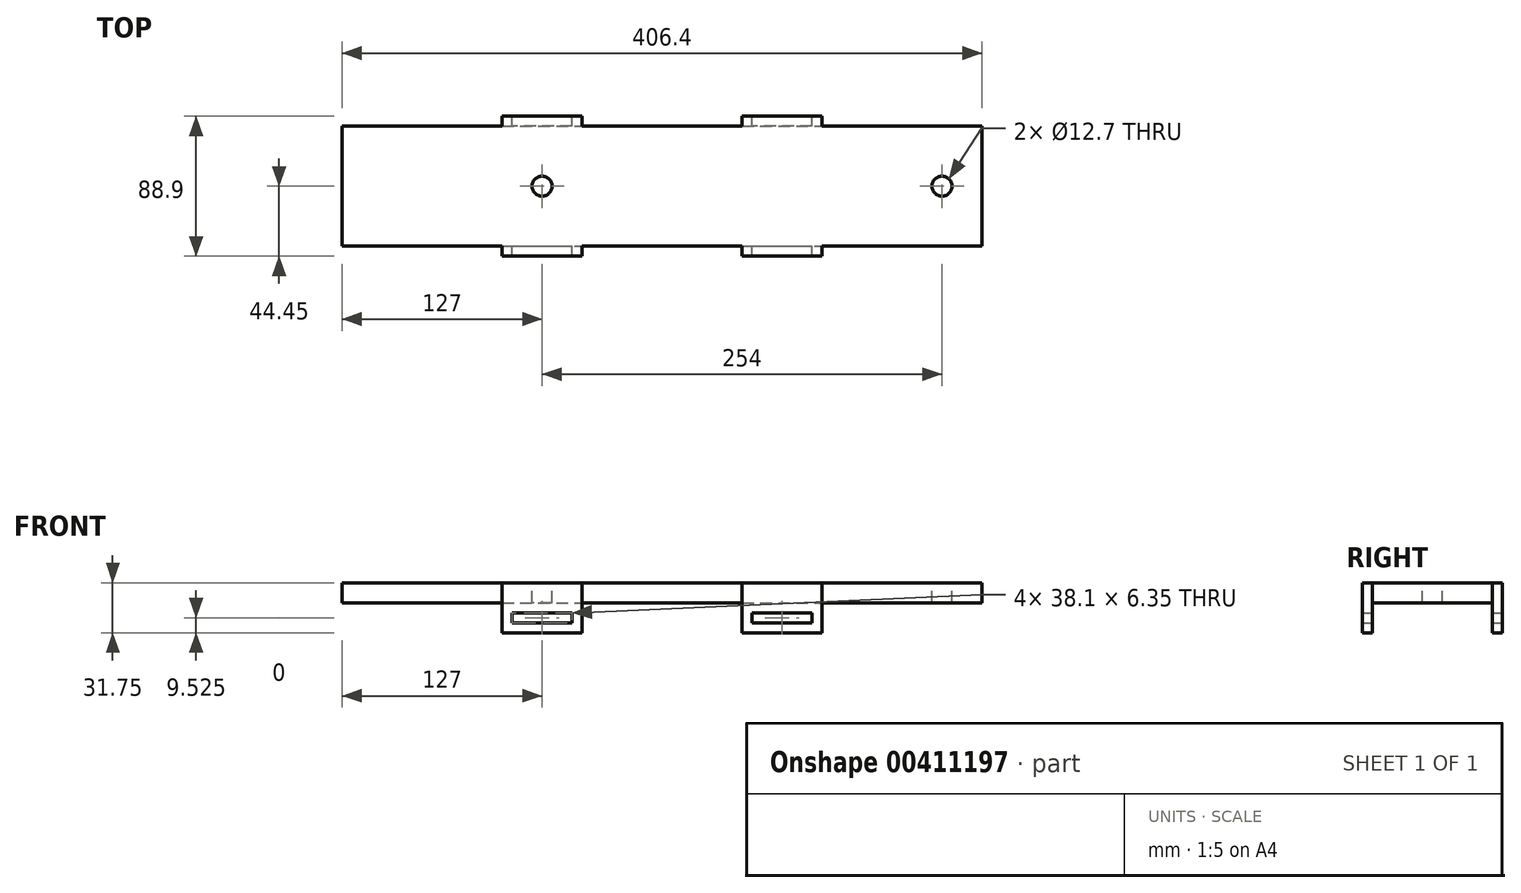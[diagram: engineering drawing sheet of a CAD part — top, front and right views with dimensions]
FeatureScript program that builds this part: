
annotation { "Feature Type Name" : "Feature", "Feature Type Description" : "" }
export const myFeature = defineFeature(function(context is Context, id is Id, definition is map)
    precondition{}
    {
        {
            var Q0;
            Q0=qCreatedBy(makeId("Top.planeOp"),FACE);
            var sketch = newSketch(context, id + "F0", { "sketchPlane" : qUnion([Q0])});
            skLineSegment(sketch, "E0.bottom", {"start": v(-203.2, 38.1) * mm, "end": v(203.2, 38.1) * mm});
            skLineSegment(sketch, "E0.top", {"start": v(-203.2, -38.1) * mm, "end": v(203.2, -38.1) * mm});
            skLineSegment(sketch, "E0.left", {"start": v(-203.2, 38.1) * mm, "end": v(-203.2, -38.1) * mm});
            skLineSegment(sketch, "E0.right", {"start": v(203.2, 38.1) * mm, "end": v(203.2, -38.1) * mm});
            skPoint(sketch, "E0.middle", {"position": v(0, 0) * mm});
            skSolve(sketch);
        }
        {
            var Q0;
            Q0 = qSketchRegion(id + "F0", true);
            extrude(context, id + "F1", {"entities" : qUnion([Q0]), "depth" : 6.35 * mm});
        }
        {
            var Q0;
            Q0=makeQuery(id+"F1.opExtrude","SWEPT_FACE",FACE,{"disambiguationData":[OSD([sQuery(id+"F0.wireOp",EDGE,"E0.top")])]});
            var sketch = newSketch(context, id + "F2", { "sketchPlane" : qUnion([Q0])});
            skLineSegment(sketch, "E1.bottom", {"start": v(50.8, 6.35) * mm, "end": v(101.6, 6.35) * mm});
            skLineSegment(sketch, "E1.top", {"start": v(50.8, -19.05) * mm, "end": v(101.6, -19.05) * mm});
            skLineSegment(sketch, "E1.left", {"start": v(50.8, 6.35) * mm, "end": v(50.8, -19.05) * mm});
            skLineSegment(sketch, "E1.right", {"start": v(101.6, 6.35) * mm, "end": v(101.6, -19.05) * mm});
            skLineSegment(sketch, "E2.bottom", {"start": v(-50.8, 6.35) * mm, "end": v(-101.6, 6.35) * mm});
            skLineSegment(sketch, "E2.top", {"start": v(-50.8, -19.05) * mm, "end": v(-101.6, -19.05) * mm});
            skLineSegment(sketch, "E2.left", {"start": v(-50.8, 6.35) * mm, "end": v(-50.8, -19.05) * mm});
            skLineSegment(sketch, "E2.right", {"start": v(-101.6, 6.35) * mm, "end": v(-101.6, -19.05) * mm});
            skSolve(sketch);
        }
        {
            var Q0;
            Q0 = qSketchRegion(id + "F2", true);
            extrude(context, id + "F3", {"entities" : qUnion([Q0]), "operationType" : NewBodyOperationType.ADD, "depth" : 6.35 * mm});
        }
        {
            var Q0;
            Q0=makeQuery(id+"F1.opExtrude","SWEPT_FACE",FACE,{"disambiguationData":[OSD([sQuery(id+"F0.wireOp",EDGE,"E0.bottom")])]});
            var sketch = newSketch(context, id + "F4", { "sketchPlane" : qUnion([Q0])});
            skLineSegment(sketch, "E3.bottom", {"start": v(-101.6, 6.35) * mm, "end": v(-50.8, 6.35) * mm});
            skLineSegment(sketch, "E3.top", {"start": v(-101.6, -19.05) * mm, "end": v(-50.8, -19.05) * mm});
            skLineSegment(sketch, "E3.left", {"start": v(-101.6, 6.35) * mm, "end": v(-101.6, -19.05) * mm});
            skLineSegment(sketch, "E3.right", {"start": v(-50.8, 6.35) * mm, "end": v(-50.8, -19.05) * mm});
            skLineSegment(sketch, "E4.bottom", {"start": v(50.8, 6.35) * mm, "end": v(101.6, 6.35) * mm});
            skLineSegment(sketch, "E4.top", {"start": v(50.8, -19.05) * mm, "end": v(101.6, -19.05) * mm});
            skLineSegment(sketch, "E4.left", {"start": v(50.8, 6.35) * mm, "end": v(50.8, -19.05) * mm});
            skLineSegment(sketch, "E4.right", {"start": v(101.6, 6.35) * mm, "end": v(101.6, -19.05) * mm});
            skSolve(sketch);
        }
        {
            var Q0;
            Q0 = qSketchRegion(id + "F4", true);
            extrude(context, id + "F5", {"entities" : qUnion([Q0]), "operationType" : NewBodyOperationType.ADD, "depth" : 6.35 * mm});
        }
        {
            var Q0;
            Q0=makeQuery(id+"F5.opExtrude","CAP_FACE",FACE,{"disambiguationData":[OSD([sQuery(id+"F4.wireOp",EDGE,"E3.bottom"),sQuery(id+"F4.wireOp",EDGE,"E3.top"),sQuery(id+"F4.wireOp",EDGE,"E3.left"),sQuery(id+"F4.wireOp",EDGE,"E3.right")])],"isStart":false});
            var sketch = newSketch(context, id + "F6", { "sketchPlane" : qUnion([Q0])});
            skLineSegment(sketch, "E5", {"start": v(-76.2, 6.35) * mm, "end": v(-76.2, -19.05) * mm, "construction": true});
            skLineSegment(sketch, "E6.bottom", {"start": v(-95.25, -12.7) * mm, "end": v(-57.15, -12.7) * mm});
            skLineSegment(sketch, "E6.top", {"start": v(-95.25, -6.35) * mm, "end": v(-57.15, -6.35) * mm});
            skLineSegment(sketch, "E6.left", {"start": v(-95.25, -12.7) * mm, "end": v(-95.25, -6.35) * mm});
            skLineSegment(sketch, "E6.right", {"start": v(-57.15, -12.7) * mm, "end": v(-57.15, -6.35) * mm});
            skPoint(sketch, "E6.middle", {"position": v(-76.2, -9.52) * mm});
            skLineSegment(sketch, "E7", {"start": v(-101.6, 0) * mm, "end": v(-50.8, 0) * mm, "construction": true});
            skSolve(sketch);
        }
        {
            var Q0;
            Q0=makeQuery(id+"F5.opExtrude","CAP_FACE",FACE,{"disambiguationData":[OSD([sQuery(id+"F4.wireOp",EDGE,"E4.bottom"),sQuery(id+"F4.wireOp",EDGE,"E4.top"),sQuery(id+"F4.wireOp",EDGE,"E4.left"),sQuery(id+"F4.wireOp",EDGE,"E4.right")])],"isStart":false});
            var sketch = newSketch(context, id + "F7", { "sketchPlane" : qUnion([Q0])});
            skLineSegment(sketch, "E8", {"start": v(76.2, 6.35) * mm, "end": v(76.2, -19.05) * mm, "construction": true});
            skLineSegment(sketch, "E9", {"start": v(50.8, 0) * mm, "end": v(101.6, 0) * mm, "construction": true});
            skLineSegment(sketch, "E10.bottom", {"start": v(57.15, -6.35) * mm, "end": v(95.25, -6.35) * mm});
            skLineSegment(sketch, "E10.top", {"start": v(57.15, -12.7) * mm, "end": v(95.25, -12.7) * mm});
            skLineSegment(sketch, "E10.left", {"start": v(57.15, -6.35) * mm, "end": v(57.15, -12.7) * mm});
            skLineSegment(sketch, "E10.right", {"start": v(95.25, -6.35) * mm, "end": v(95.25, -12.7) * mm});
            skPoint(sketch, "E10.middle", {"position": v(76.2, -9.52) * mm});
            skSolve(sketch);
        }
        {
            var Q0;
            Q0=makeQuery(id+"F7.imprint","IMPRINT",FACE,{"disambiguationData":[TD([[makeQuery(id+"F7.imprint","IMPRINT",EDGE,{"derivedFrom":sQuery(id+"F7.wireOp",EDGE,"E10.bottom")}),-1.0]])]});
            var Q1;
            Q1=makeQuery(id+"F6.imprint","IMPRINT",FACE,{"disambiguationData":[TD([[makeQuery(id+"F6.imprint","IMPRINT",EDGE,{"derivedFrom":sQuery(id+"F6.wireOp",EDGE,"E6.bottom")}),1.0]])]});
            extrude(context, id + "F8", {"entities" : qUnion([Q0, Q1]), "operationType" : NewBodyOperationType.REMOVE, "endBound" : BoundingType.THROUGH_ALL, "oppositeDirection" : true, "depth" : 25.4 * mm});
        }
        {
            var Q0;
            Q0=makeQuery(id+"F5.boolean.opBoolean","MERGE",FACE,{"derivedFrom":[makeQuery(id+"F3.boolean.opBoolean","MERGE",FACE,{"derivedFrom":[makeQuery(id+"F1.opExtrude","CAP_FACE",FACE,{"disambiguationData":[OSD([sQuery(id+"F0.wireOp",EDGE,"E0.bottom"),sQuery(id+"F0.wireOp",EDGE,"E0.top"),sQuery(id+"F0.wireOp",EDGE,"E0.left"),sQuery(id+"F0.wireOp",EDGE,"E0.right")])],"isStart":false}),makeQuery(id+"F3.opExtrude","SWEPT_FACE",FACE,{"disambiguationData":[OSD([sQuery(id+"F2.wireOp",EDGE,"E1.bottom")])]}),makeQuery(id+"F3.opExtrude","SWEPT_FACE",FACE,{"disambiguationData":[OSD([sQuery(id+"F2.wireOp",EDGE,"E2.bottom")])]})]}),makeQuery(id+"F5.opExtrude","SWEPT_FACE",FACE,{"disambiguationData":[OSD([sQuery(id+"F4.wireOp",EDGE,"E3.bottom")])]}),makeQuery(id+"F5.opExtrude","SWEPT_FACE",FACE,{"disambiguationData":[OSD([sQuery(id+"F4.wireOp",EDGE,"E4.bottom")])]})]});
            var sketch = newSketch(context, id + "F9", { "sketchPlane" : qUnion([Q0])});
            skLineSegment(sketch, "E11", {"start": v(-203.2, 38.1) * mm, "end": v(-101.6, 38.1) * mm});
            skLineSegment(sketch, "E12", {"start": v(-101.6, 38.1) * mm, "end": v(-101.6, 44.45) * mm});
            skLineSegment(sketch, "E13", {"start": v(-101.6, 44.45) * mm, "end": v(-50.8, 44.45) * mm});
            skLineSegment(sketch, "E14", {"start": v(-50.8, 44.45) * mm, "end": v(-50.8, 38.1) * mm});
            skLineSegment(sketch, "E15", {"start": v(-50.8, 38.1) * mm, "end": v(50.8, 38.1) * mm});
            skLineSegment(sketch, "E16", {"start": v(50.8, 38.1) * mm, "end": v(50.8, 44.45) * mm});
            skLineSegment(sketch, "E17", {"start": v(50.8, 44.45) * mm, "end": v(101.6, 44.45) * mm});
            skLineSegment(sketch, "E18", {"start": v(101.6, 44.45) * mm, "end": v(101.6, 38.1) * mm});
            skLineSegment(sketch, "E19", {"start": v(101.6, 38.1) * mm, "end": v(203.2, 38.1) * mm});
            skLineSegment(sketch, "E20", {"start": v(203.2, 38.1) * mm, "end": v(203.2, -38.1) * mm});
            skLineSegment(sketch, "E21", {"start": v(203.2, -38.1) * mm, "end": v(101.6, -38.1) * mm});
            skLineSegment(sketch, "E22", {"start": v(101.6, -38.1) * mm, "end": v(101.6, -44.45) * mm});
            skLineSegment(sketch, "E23", {"start": v(101.6, -44.45) * mm, "end": v(50.8, -44.45) * mm});
            skLineSegment(sketch, "E24", {"start": v(50.8, -44.45) * mm, "end": v(50.8, -38.1) * mm});
            skLineSegment(sketch, "E25", {"start": v(50.8, -38.1) * mm, "end": v(-50.8, -38.1) * mm});
            skLineSegment(sketch, "E26", {"start": v(-50.8, -38.1) * mm, "end": v(-50.8, -44.45) * mm});
            skLineSegment(sketch, "E27", {"start": v(-50.8, -44.45) * mm, "end": v(-101.6, -44.45) * mm});
            skLineSegment(sketch, "E28", {"start": v(-101.6, -44.45) * mm, "end": v(-101.6, -38.1) * mm});
            skLineSegment(sketch, "E29", {"start": v(-101.6, -38.1) * mm, "end": v(-203.2, -38.1) * mm});
            skLineSegment(sketch, "E30", {"start": v(-203.2, -38.1) * mm, "end": v(-203.2, 38.1) * mm});
            skSolve(sketch);
        }
        {
            var Q0;
            Q0 = qSketchRegion(id + "F9", true);
            extrude(context, id + "F10", {"entities" : qUnion([Q0]), "operationType" : NewBodyOperationType.ADD, "depth" : 6.35 * mm});
        }
        {
            var Q0;
            Q0=makeQuery(id+"F10.opExtrude","CAP_FACE",FACE,{"disambiguationData":[OSD([sQuery(id+"F9.wireOp",EDGE,"E11"),sQuery(id+"F9.wireOp",EDGE,"E12"),sQuery(id+"F9.wireOp",EDGE,"E13"),sQuery(id+"F9.wireOp",EDGE,"E14"),sQuery(id+"F9.wireOp",EDGE,"E15"),sQuery(id+"F9.wireOp",EDGE,"E16"),sQuery(id+"F9.wireOp",EDGE,"E17"),sQuery(id+"F9.wireOp",EDGE,"E18"),sQuery(id+"F9.wireOp",EDGE,"E19"),sQuery(id+"F9.wireOp",EDGE,"E20"),sQuery(id+"F9.wireOp",EDGE,"E21"),sQuery(id+"F9.wireOp",EDGE,"E22"),sQuery(id+"F9.wireOp",EDGE,"E23"),sQuery(id+"F9.wireOp",EDGE,"E24"),sQuery(id+"F9.wireOp",EDGE,"E25"),sQuery(id+"F9.wireOp",EDGE,"E26"),sQuery(id+"F9.wireOp",EDGE,"E27"),sQuery(id+"F9.wireOp",EDGE,"E28"),sQuery(id+"F9.wireOp",EDGE,"E29"),sQuery(id+"F9.wireOp",EDGE,"E30")])],"isStart":false});
            var sketch = newSketch(context, id + "F11", { "sketchPlane" : qUnion([Q0])});
            skCircle(sketch, "E31", {"center": v(177.8, 0) * mm, "radius": 6.35 * mm});
            skCircle(sketch, "E32", {"center": v(-76.2, 0) * mm, "radius": 6.35 * mm});
            skSolve(sketch);
        }
        {
            var Q0;
            Q0=sQuery(id+"F11.wireOp",VERTEX,"E31.center");
            var Q1;
            Q1=sQuery(id+"F11.wireOp",VERTEX,"E32.center");
            var Q2;
            Q2=makeQuery(id+"F1.opExtrude","SWEPT_BODY",BODY,{"disambiguationData":[OSD([sQuery(id+"F0.wireOp",EDGE,"E0.bottom"),sQuery(id+"F0.wireOp",EDGE,"E0.top"),sQuery(id+"F0.wireOp",EDGE,"E0.left"),sQuery(id+"F0.wireOp",EDGE,"E0.right")])]});
            hole(context, id + "F12", {"style" : HoleStyle.SIMPLE, "endStyle" : HoleEndStyle.THROUGH, "holeDiameter" : 12.7 * mm, "isTappedThrough" : true, "tappedDepth" : 12.7 * mm, "tapClearance" : 3, "locations" : qUnion([Q0, Q1]), "scope" : qUnion([Q2])});
        }
    });
